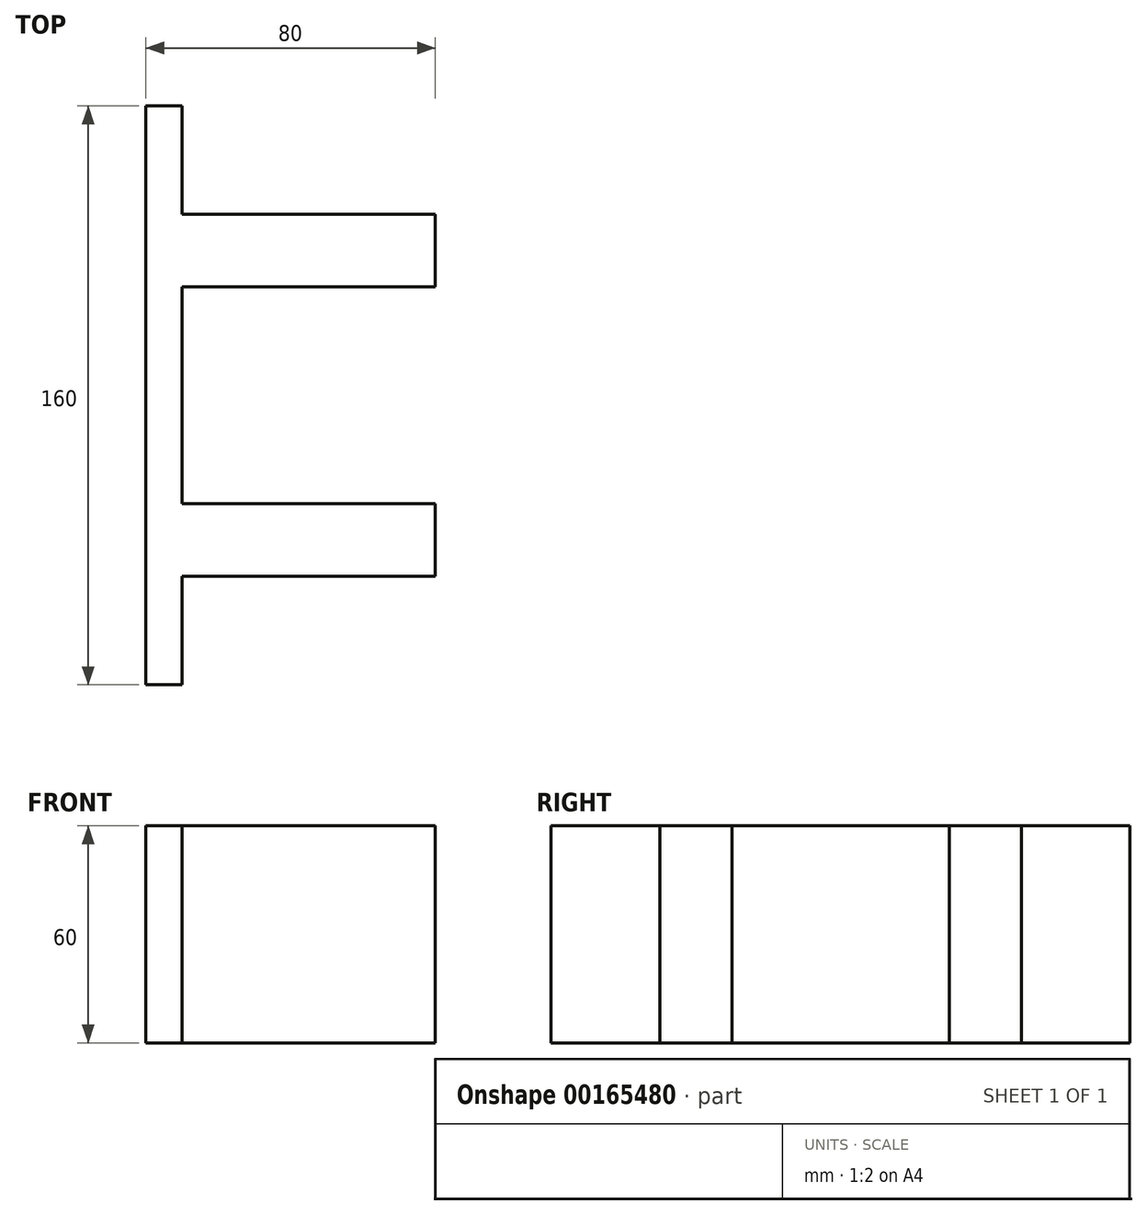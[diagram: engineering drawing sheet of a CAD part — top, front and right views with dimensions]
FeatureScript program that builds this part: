
annotation { "Feature Type Name" : "Feature", "Feature Type Description" : "" }
export const myFeature = defineFeature(function(context is Context, id is Id, definition is map)
    precondition{}
    {
        {
            var Q0;
            Q0=qCreatedBy(makeId("Front.planeOp"),FACE);
            var sketch = newSketch(context, id + "F0", { "sketchPlane" : qUnion([Q0])});
            skLineSegment(sketch, "E0.bottom", {"start": v(10, 30) * mm, "end": v(-40, 30) * mm});
            skLineSegment(sketch, "E0.top", {"start": v(40, -30) * mm, "end": v(-40, -30) * mm});
            skLineSegment(sketch, "E0.left", {"start": v(40, 0) * mm, "end": v(40, -30) * mm});
            skLineSegment(sketch, "E0.right", {"start": v(-40, 30) * mm, "end": v(-40, -30) * mm});
            skPoint(sketch, "E0.middle", {"position": v(0, 0) * mm});
            skLineSegment(sketch, "E1", {"start": v(10, 30) * mm, "end": v(40, 0) * mm});
            skPoint(sketch, "E2.orphan", {"position": v(40, 30) * mm});
            skSolve(sketch);
        }
        {
            var Q0;
            Q0 = qSketchRegion(id + "F0", true);
            extrude(context, id + "F1", {"entities" : qUnion([Q0]), "depth" : 10 * mm});
        }
        {
            var Q0;
            Q0=makeQuery(id+"F1.opExtrude","CAP_FACE",FACE,{"disambiguationData":[OSD([sQuery(id+"F0.wireOp",EDGE,"E0.bottom"),sQuery(id+"F0.wireOp",EDGE,"E0.top"),sQuery(id+"F0.wireOp",EDGE,"E0.left"),sQuery(id+"F0.wireOp",EDGE,"E0.right"),sQuery(id+"F0.wireOp",EDGE,"E1")])],"isStart":false});
            var sketch = newSketch(context, id + "F2", { "sketchPlane" : qUnion([Q0])});
            skLineSegment(sketch, "E3", {"start": v(-30, 30) * mm, "end": v(-30, -30) * mm});
            skSolve(sketch);
        }
        {
            var Q0;
            Q0 = qSketchRegion(id + "F2", true);
            var Q1;
            {var subQ0=sQuery(id+"F2.wireOp",EDGE,"E3");Q1=makeQuery(id+"F2.imprint","IMPRINT",FACE,{"disambiguationData":[TD([[makeQuery(id+"F2.imprint","IMPRINT",EDGE,{"derivedFrom":subQ0}),-1.0]])]});}
            extrude(context, id + "F3", {"entities" : qUnion([Q0, Q1]), "operationType" : NewBodyOperationType.ADD, "depth" : 30 * mm});
        }
        {
            var Q0;
            Q0=makeQuery(id+"F1.opExtrude","SWEPT_BODY",BODY,{"disambiguationData":[OSD([sQuery(id+"F0.wireOp",EDGE,"E0.bottom"),sQuery(id+"F0.wireOp",EDGE,"E0.top"),sQuery(id+"F0.wireOp",EDGE,"E0.left"),sQuery(id+"F0.wireOp",EDGE,"E0.right"),sQuery(id+"F0.wireOp",EDGE,"E1")])]});
            var Q1;
            Q1=qCreatedBy(makeId("Top.planeOp"),FACE);
            mirror(context, id + "F4", {"operationType" : NewBodyOperationType.ADD, "entities" : qUnion([Q0]), "mirrorPlane" : qUnion([Q1])});
        }
        {
            var Q0;
            Q0=makeQuery(id+"F1.opExtrude","SWEPT_BODY",BODY,{"disambiguationData":[OSD([sQuery(id+"F0.wireOp",EDGE,"E0.bottom"),sQuery(id+"F0.wireOp",EDGE,"E0.top"),sQuery(id+"F0.wireOp",EDGE,"E0.left"),sQuery(id+"F0.wireOp",EDGE,"E0.right"),sQuery(id+"F0.wireOp",EDGE,"E1")])]});
            var Q1;
            {var subQ0=makeQuery(id+"F1.opExtrude","CAP_FACE",FACE,{"disambiguationData":[OSD([sQuery(id+"F0.wireOp",EDGE,"E0.bottom"),sQuery(id+"F0.wireOp",EDGE,"E0.top"),sQuery(id+"F0.wireOp",EDGE,"E0.left"),sQuery(id+"F0.wireOp",EDGE,"E0.right"),sQuery(id+"F0.wireOp",EDGE,"E1")])],"isStart":true});Q1=makeQuery(id+"F4.boolean.opBoolean","MERGE",FACE,{"derivedFrom":[subQ0,makeQuery(id+"F4.opPattern","COPY",FACE,{"derivedFrom":subQ0,"instanceName":"1"})]});}
            mirror(context, id + "F5", {"operationType" : NewBodyOperationType.ADD, "entities" : qUnion([Q0]), "mirrorPlane" : qUnion([Q1])});
        }
        {
            var Q0;
            Q0=makeQuery(id+"F1.opExtrude","SWEPT_BODY",BODY,{"disambiguationData":[OSD([sQuery(id+"F0.wireOp",EDGE,"E0.bottom"),sQuery(id+"F0.wireOp",EDGE,"E0.top"),sQuery(id+"F0.wireOp",EDGE,"E0.left"),sQuery(id+"F0.wireOp",EDGE,"E0.right"),sQuery(id+"F0.wireOp",EDGE,"E1")])]});
            var Q1;
            Q1=makeQuery(id+"F5.opPattern","COPY",FACE,{"derivedFrom":makeQuery(id+"F3.opExtrude","CAP_FACE",FACE,{"disambiguationData":[OSD([sQuery(id+"F0.wireOp",EDGE,"E0.bottom"),sQuery(id+"F0.wireOp",EDGE,"E0.top"),sQuery(id+"F0.wireOp",EDGE,"E0.right"),sQuery(id+"F2.wireOp",EDGE,"E3")])],"isStart":false}),"instanceName":"1"});
            mirror(context, id + "F6", {"operationType" : NewBodyOperationType.ADD, "entities" : qUnion([Q0]), "mirrorPlane" : qUnion([Q1])});
        }
    });
